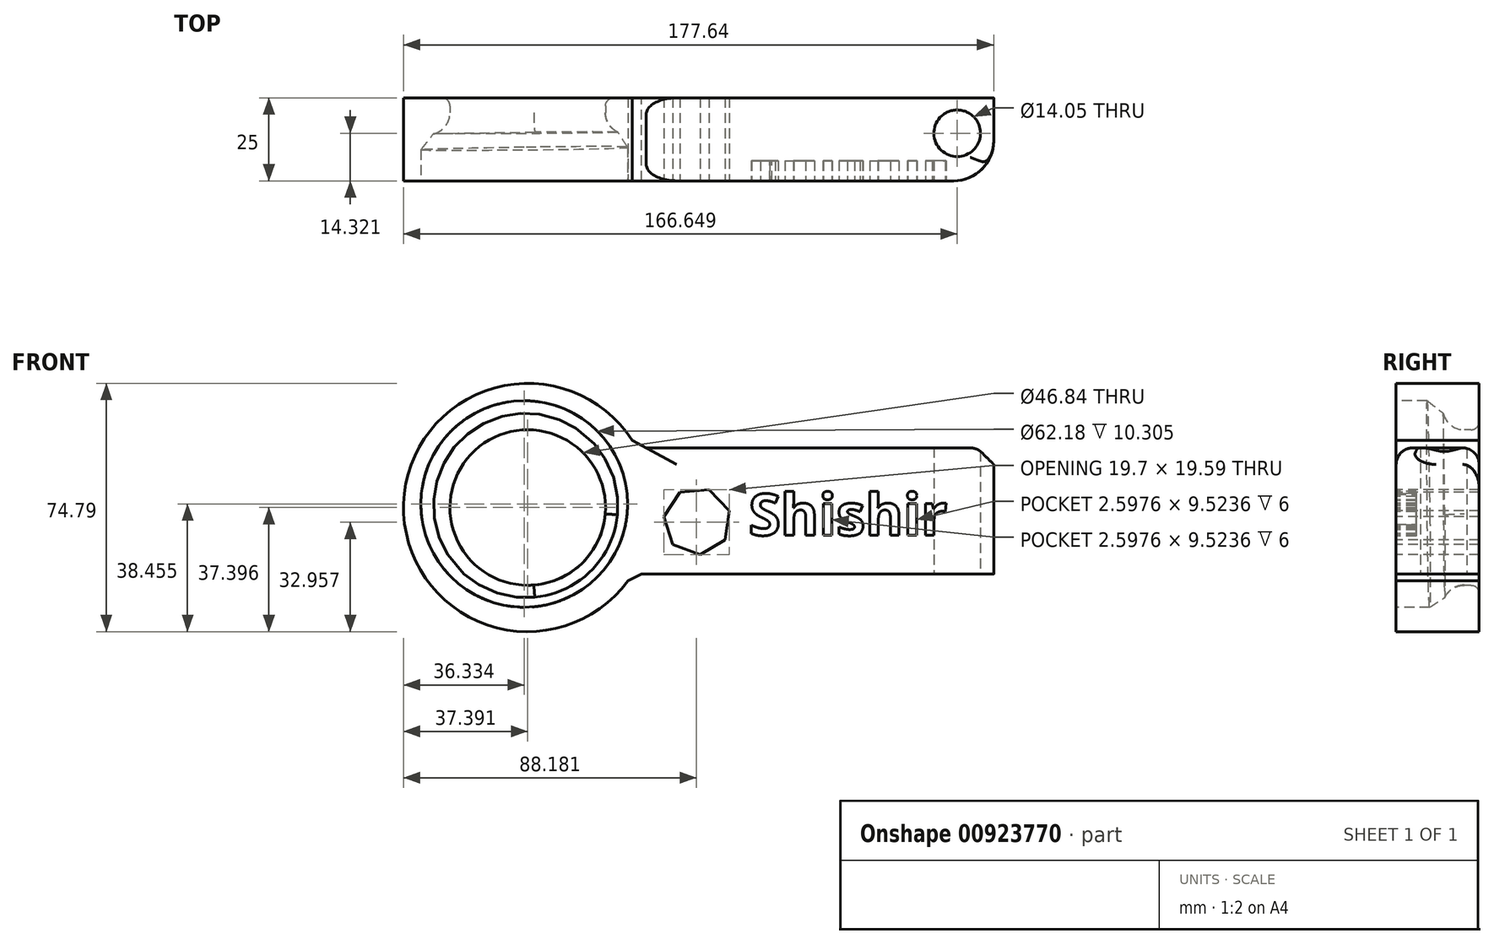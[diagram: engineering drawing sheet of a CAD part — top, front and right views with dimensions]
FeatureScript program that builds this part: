
annotation { "Feature Type Name" : "Feature", "Feature Type Description" : "" }
export const myFeature = defineFeature(function(context is Context, id is Id, definition is map)
    precondition{}
    {
        {
            var Q0;
            Q0=qCreatedBy(makeId("Front.planeOp"),FACE);
            var sketch = newSketch(context, id + "F0", { "sketchPlane" : qUnion([Q0])});
            skCircle(sketch, "E0", {"center": v(-140.25, 20.04) * mm, "radius": 23.42 * mm});
            skCircle(sketch, "E1", {"center": v(-140.25, 20.04) * mm, "radius": 37.4 * mm});
            skLineSegment(sketch, "E2.bottom", {"start": v(-108.68, 38) * mm, "end": v(0, 38) * mm});
            skLineSegment(sketch, "E2.top", {"start": v(-108.68, 0) * mm, "end": v(0, 0) * mm});
            skLineSegment(sketch, "E2.left", {"start": v(-108.68, 38) * mm, "end": v(-108.68, 0) * mm});
            skLineSegment(sketch, "E2.right", {"start": v(0, 38) * mm, "end": v(0, 0) * mm});
            skSolve(sketch);
        }
        {
            var Q0;
            Q0 = qSketchRegion(id + "F0", true);
            extrude(context, id + "F1", {"entities" : qUnion([Q0]), "oppositeDirection" : true, "depth" : 25 * mm, "offsetDistance" : 25 * mm});
        }
        {
            var Q0;
            Q0=qCreatedBy(makeId("Front.planeOp"),FACE);
            var sketch = newSketch(context, id + "F2", { "sketchPlane" : qUnion([Q0])});
            skCircle(sketch, "E3", {"center": v(-141.3, 21.1) * mm, "radius": 31.1 * mm});
            skSolve(sketch);
        }
        {
            var Q0;
            Q0 = qSketchRegion(id + "F2", true);
            extrude(context, id + "F3", {"entities" : qUnion([Q0]), "operationType" : NewBodyOperationType.REMOVE, "oppositeDirection" : true, "depth" : 14 * mm, "offsetDistance" : 25 * mm});
        }
        {
            var Q0;
            Q0=makeQuery(id+"F1.opExtrude","SWEPT_EDGE",EDGE,{"disambiguationData":[OSD([sQuery(id+"F0.wireOp",EDGE,"E2.bottom"),sQuery(id+"F0.wireOp",EDGE,"E2.left")])]});
            chamfer(context, id + "F4", {"entities" : qUnion([Q0]), "width" : 5 * mm, "tangentPropagation" : true});
        }
        {
            var Q0;
            Q0=makeQuery(id+"F1.opExtrude","SWEPT_EDGE",EDGE,{"disambiguationData":[OSD([sQuery(id+"F0.wireOp",EDGE,"E2.top"),sQuery(id+"F0.wireOp",EDGE,"E2.left")])]});
            chamfer(context, id + "F5", {"entities" : qUnion([Q0]), "width" : 5 * mm, "tangentPropagation" : true});
        }
        {
            var Q0;
            Q0=makeQuery(id+"F3.boolean.opBoolean","COPY",EDGE,{"derivedFrom":makeQuery(id+"F3.opExtrude","CAP_EDGE",EDGE,{"disambiguationData":[OSD([sQuery(id+"F2.wireOp",EDGE,"E3")])],"isStart":true})});
            var Q1;
            Q1=makeQuery(id+"F3.boolean.opBoolean","INTERSECT",EDGE,{"derivedFrom":[makeQuery(id+"F1.opExtrude","SWEPT_FACE",FACE,{"disambiguationData":[OSD([sQuery(id+"F0.wireOp",EDGE,"E0")])]}),makeQuery(id+"F3.opExtrude","CAP_FACE",FACE,{"disambiguationData":[OSD([sQuery(id+"F2.wireOp",EDGE,"E3")])],"isStart":false})]});
            fillet(context, id + "F6", {"entities" : qUnion([Q0, Q1]), "radius" : 6.52 * mm, "tangentPropagation" : true, "allowEdgeOverflow" : false});
        }
        {
            var Q0;
            Q0=makeQuery(id+"F3.boolean.opBoolean","COPY",EDGE,{"derivedFrom":makeQuery(id+"F3.opExtrude","CAP_EDGE",EDGE,{"disambiguationData":[OSD([sQuery(id+"F2.wireOp",EDGE,"E3")])],"isStart":false})});
            var Q1;
            {var subQ0=sQuery(id+"F2.wireOp",EDGE,"E3");Q1=makeQuery(id+"F6.opFillet","BLEND_EDGE",EDGE,{"blendedFrom":[makeQuery(id+"F3.boolean.opBoolean","COPY",EDGE,{"derivedFrom":makeQuery(id+"F3.opExtrude","CAP_EDGE",EDGE,{"disambiguationData":[OSD([subQ0])],"isStart":true})}),makeQuery(id+"F3.boolean.opBoolean","COPY",FACE,{"derivedFrom":makeQuery(id+"F3.opExtrude","SWEPT_FACE",FACE,{"disambiguationData":[OSD([subQ0])]})})],"blendedInto":[makeQuery(id+"F3.boolean.opBoolean","COPY",FACE,{"derivedFrom":makeQuery(id+"F3.opExtrude","SWEPT_FACE",FACE,{"disambiguationData":[OSD([subQ0])]})})]});}
            chamfer(context, id + "F7", {"entities" : qUnion([Q0, Q1]), "width" : 5 * mm, "tangentPropagation" : true});
        }
        {
            var Q0;
            Q0=makeQuery(id+"F1.opExtrude","CAP_EDGE",EDGE,{"disambiguationData":[OSD([sQuery(id+"F0.wireOp",EDGE,"E2.right")])],"isStart":true});
            fillet(context, id + "F8", {"entities" : qUnion([Q0]), "radius" : 12.07 * mm, "tangentPropagation" : true, "allowEdgeOverflow" : false});
        }
        {
            var Q0;
            Q0=makeQuery(id+"F1.opExtrude","SWEPT_FACE",FACE,{"disambiguationData":[OSD([sQuery(id+"F0.wireOp",EDGE,"E2.right")])]});
            fillet(context, id + "F9", {"entities" : qUnion([Q0]), "radius" : 0.02 * mm, "tangentPropagation" : true, "allowEdgeOverflow" : false});
        }
        {
            var Q0;
            {var subQ0=makeQuery(id+"F1.opExtrude","SWEPT_FACE",FACE,{"disambiguationData":[OSD([sQuery(id+"F0.wireOp",EDGE,"E0")])]});Q0=makeQuery(id+"F6.opFillet","BLEND_EDGE",EDGE,{"disambiguationData":[OD(1.0)],"blendedFrom":[makeQuery(id+"F3.boolean.opBoolean","INTERSECT",EDGE,{"derivedFrom":[subQ0,makeQuery(id+"F3.opExtrude","CAP_FACE",FACE,{"disambiguationData":[OSD([sQuery(id+"F2.wireOp",EDGE,"E3")])],"isStart":false})]}),subQ0],"blendedInto":[subQ0]});}
            var Q1;
            Q1=makeQuery(id+"F1.opExtrude","CAP_EDGE",EDGE,{"disambiguationData":[OSD([sQuery(id+"F0.wireOp",EDGE,"E0")])],"isStart":false});
            fillet(context, id + "F10", {"entities" : qUnion([Q0, Q1]), "radius" : 2.41 * mm, "tangentPropagation" : true, "allowEdgeOverflow" : false});
        }
        {
            var Q0;
            Q0=qCreatedBy(makeId("Front.planeOp"),FACE);
            var sketch = newSketch(context, id + "F11", { "sketchPlane" : qUnion([Q0])});
            skText(sketch, "E4", { "text": "Shishir", "fontName": "OpenSans-Bold.ttf"});
            const initialGuessF11  = {"E4": [-0.07375, 0.01166, 1, 0, 0.01256]};
            skSetInitialGuess(sketch, initialGuessF11);
            skSolve(sketch);
        }
        {
            var Q0;
            Q0 = qSketchRegion(id + "F11", true);
            extrude(context, id + "F12", {"entities" : qUnion([Q0]), "operationType" : NewBodyOperationType.REMOVE, "oppositeDirection" : true, "depth" : 6 * mm, "offsetDistance" : 25 * mm});
        }
        {
            var Q0;
            Q0=qCreatedBy(makeId("Top.planeOp"),FACE);
            var sketch = newSketch(context, id + "F13", { "sketchPlane" : qUnion([Q0])});
            skCircle(sketch, "E5", {"center": v(-11, 14.32) * mm, "radius": 7.02 * mm});
            skSolve(sketch);
        }
        {
            var Q0;
            Q0=makeQuery(id+"F13.imprint","IMPRINT",FACE,{"disambiguationData":[TD([[makeQuery(id+"F13.imprint","IMPRINT",EDGE,{"derivedFrom":sQuery(id+"F13.wireOp",EDGE,"E5")}),1.0]])]});
            extrude(context, id + "F14", {"entities" : qUnion([Q0]), "operationType" : NewBodyOperationType.REMOVE, "depth" : 81 * mm, "offsetDistance" : 25 * mm});
        }
        {
            var Q0;
            Q0=makeQuery(id+"F8.opFillet","BLEND_FACE",FACE,{"disambiguationData":[OSD([sQuery(id+"F0.wireOp",EDGE,"E2.right")])]});
            fillet(context, id + "F15", {"entities" : qUnion([Q0]), "radius" : 5 * mm, "tangentPropagation" : true, "allowEdgeOverflow" : false});
        }
        {
            var Q0;
            Q0=makeQuery(id+"F4.opChamfer","BLEND_FACE",FACE,{"disambiguationData":[OSD([sQuery(id+"F0.wireOp",EDGE,"E2.bottom"),sQuery(id+"F0.wireOp",EDGE,"E2.right")])]});
            fillet(context, id + "F16", {"entities" : qUnion([Q0]), "radius" : 5 * mm, "tangentPropagation" : true, "allowEdgeOverflow" : false});
        }
        {
            var Q0;
            Q0=qCreatedBy(makeId("Front.planeOp"),FACE);
            var sketch = newSketch(context, id + "F17", { "sketchPlane" : qUnion([Q0])});
            skCircle(sketch, "E6.cCircle", {"center": v(-89.26, 15.9) * mm, "radius": 9.14 * mm, "construction": true});
            skLineSegment(sketch, "E6.0", {"start": v(-96.62, 8.92) * mm, "end": v(-99.3, 17.3) * mm});
            skLineSegment(sketch, "E6.1", {"start": v(-99.3, 17.3) * mm, "end": v(-94.44, 24.63) * mm});
            skLineSegment(sketch, "E6.2", {"start": v(-94.44, 24.63) * mm, "end": v(-85.67, 25.39) * mm});
            skLineSegment(sketch, "E6.3", {"start": v(-85.67, 25.39) * mm, "end": v(-79.6, 19) * mm});
            skLineSegment(sketch, "E6.4", {"start": v(-79.6, 19) * mm, "end": v(-80.82, 10.3) * mm});
            skLineSegment(sketch, "E6.5", {"start": v(-80.82, 10.3) * mm, "end": v(-88.39, 5.8) * mm});
            skLineSegment(sketch, "E6.6", {"start": v(-88.39, 5.8) * mm, "end": v(-96.62, 8.92) * mm});
            skPoint(sketch, "E6.0.midPoint", {"position": v(-97.96, 13.11) * mm});
            skSolve(sketch);
        }
        {
            var Q0;
            Q0=makeQuery(id+"F17.imprint","IMPRINT",FACE,{"disambiguationData":[TD([[makeQuery(id+"F17.imprint","IMPRINT",EDGE,{"derivedFrom":sQuery(id+"F17.wireOp",EDGE,"E6.0")}),-1.0]])]});
            extrude(context, id + "F18", {"entities" : qUnion([Q0]), "operationType" : NewBodyOperationType.REMOVE, "oppositeDirection" : true, "depth" : 50 * mm, "offsetDistance" : 25 * mm});
        }
    });
